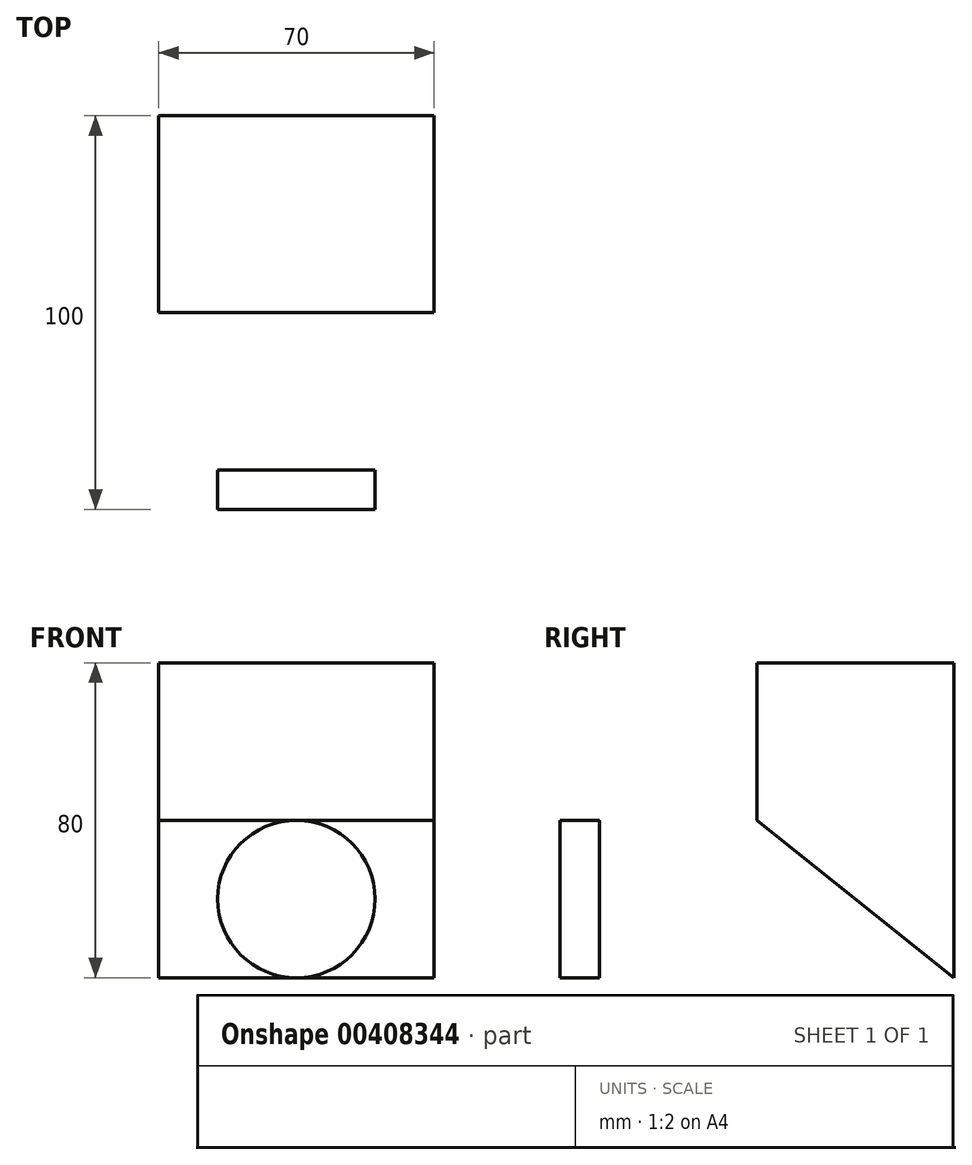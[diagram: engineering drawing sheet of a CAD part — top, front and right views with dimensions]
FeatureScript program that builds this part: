
annotation { "Feature Type Name" : "Feature", "Feature Type Description" : "" }
export const myFeature = defineFeature(function(context is Context, id is Id, definition is map)
    precondition{}
    {
        {
            var Q0;
            Q0=qCreatedBy(makeId("Right.planeOp"),FACE);
            var sketch = newSketch(context, id + "F0", { "sketchPlane" : qUnion([Q0])});
            skLineSegment(sketch, "E0.bottom", {"start": v(0, 0) * mm, "end": v(0, 0) * mm});
            skLineSegment(sketch, "E0.top", {"start": v(0, 40) * mm, "end": v(0, 40) * mm});
            skLineSegment(sketch, "E0.left", {"start": v(0, 0) * mm, "end": v(0, 40) * mm});
            skLineSegment(sketch, "E0.right", {"start": v(0, 0) * mm, "end": v(0, 40) * mm});
            skLineSegment(sketch, "E1.bottom", {"start": v(0, 40) * mm, "end": v(50, 40) * mm});
            skLineSegment(sketch, "E1.top", {"start": v(0, 40) * mm, "end": v(50, 40) * mm});
            skLineSegment(sketch, "E1.right", {"start": v(50, 40) * mm, "end": v(50, 40) * mm});
            skLineSegment(sketch, "E2", {"start": v(50, 40) * mm, "end": v(50, -40) * mm});
            skLineSegment(sketch, "E3", {"start": v(50, -40) * mm, "end": v(0, 0) * mm});
            skSolve(sketch);
        }
        {
            var Q0;
            Q0 = qSketchRegion(id + "F0", true);
            extrude(context, id + "F1", {"entities" : qUnion([Q0]), "endBound" : BoundingType.SYMMETRIC, "depth" : 70 * mm});
        }
        {
            var Q0;
            Q0=qCreatedBy(makeId("Front.planeOp"),FACE);
            cPlane(context, id + "F2", {"entities" : qUnion([Q0]), "cplaneType" : CPlaneType.OFFSET, "offset" : 50 * mm, "width" : 150 * mm, "height" : 150 * mm});
        }
        {
            var Q0;
            Q0=qCreatedBy(id+"F2.planeOp",FACE);
            var sketch = newSketch(context, id + "F3", { "sketchPlane" : qUnion([Q0])});
            skLineSegment(sketch, "E4.0", {"start": v(35, -40) * mm, "end": v(-35, -40) * mm});
            skLineSegment(sketch, "E5.0", {"start": v(35, 0) * mm, "end": v(-35, 0) * mm});
            skCircle(sketch, "E6", {"center": v(0, -20) * mm, "radius": 20 * mm});
            skSolve(sketch);
        }
        {
            var Q0;
            Q0 = qSketchRegion(id + "F3", true);
            extrude(context, id + "F4", {"entities" : qUnion([Q0]), "oppositeDirection" : true, "depth" : 10 * mm});
        }
    });
